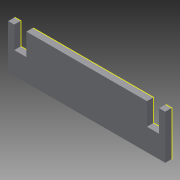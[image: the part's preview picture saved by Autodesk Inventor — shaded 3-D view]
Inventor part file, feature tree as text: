
AUTODESK INVENTOR PART (.ipt)
format: ipt  version: 2014 SP1 (Build 180222100, 222)  size: 113,152 bytes
history: native  units: mm
features: sketch x3, extrude x2
ambient origin geometry x8: Origin, YZ Plane, XZ Plane, XY Plane, X Axis, Y Axis, Z Axis, Center Point
bodies: Solid1 (feature_tree)
feature tree (5):
  extrude  "Extrusion1"  Depth=3.0mm TaperAngle=0.0deg
  extrude  "Extrusion2"  Depth=5.5mm
  sketch  "Sketch4"  dims[d7=10.0mm d8=30.0mm d9=3.0mm d10=0.0mm]
  sketch  "Sketch1"  dims[d0=71.0mm d1=3.0mm d2=0.0mm]
  sketch  "Sketch3"  dims[d5=20.0mm d6=5.5mm]
